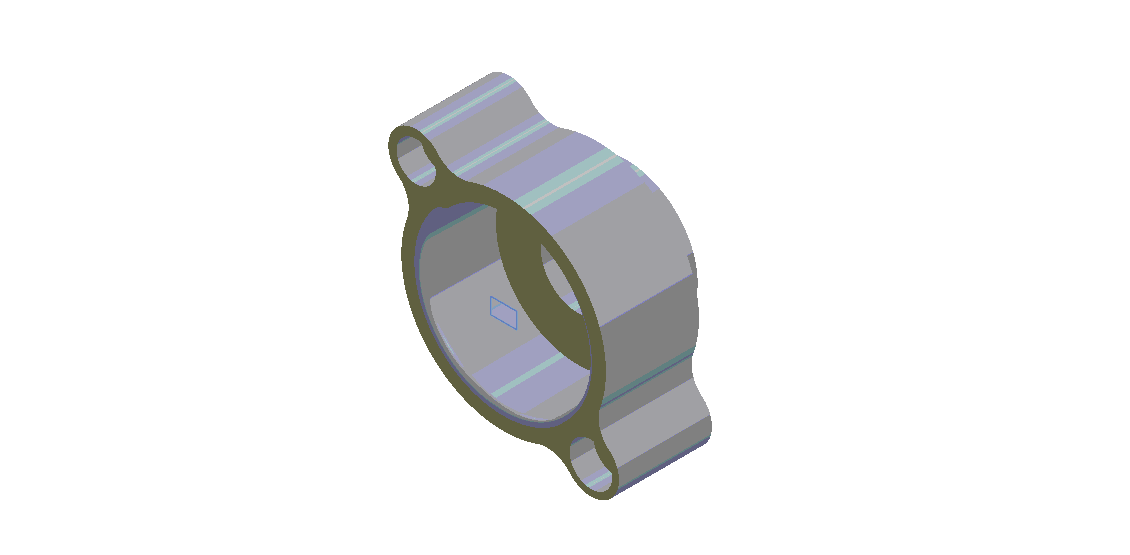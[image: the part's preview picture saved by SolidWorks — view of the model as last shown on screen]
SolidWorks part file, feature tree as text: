
SOLIDWORKS PART (.sldprt)
format: sldprt  version: not decoded by parser v0  size: 208,896 bytes
history: native  units: mm
features: sketch x8, plane x4, extrude x2, cut_extrude x2, hole x2, material x1, fillet x1 (+10 scaffold rows collapsed)
feature tree (30):
  scaffold x10  (default folders/planes/origin — collapsed)
  material  "Matériau <non spécifié>"
  plane  "FRONT"
  plane  "TOP"
  plane  "RIGHT"
  plane  "Plan1"  Offset=838.2mm
  sketch  "Esquisse1"
  extrude  "Boss.-Extru.1"  Depth=635mm
  sketch  "Esquisse2"
  extrude  "Boss.-Extru.2"  Depth=203.2mm
  sketch  "Esquisse3"
  cut_extrude  "Enlèv. mat.-Extru.1"  Depth=508mm
  sketch  "Esquisse4"
  cut_extrude  "Enlèv. mat.-Extru.2"  Depth=330.2mm
  hole  "Perçage1"  Diameter=139.7mm Depth=838.2mm
  sketch  "Esquisse6"
  sketch  "Esquisse5"  dims[Diamètre=139.7mm Profondeur=838.2mm Diamètre chambrage=292.1mm Profondeur chambrage=165.1mm]
  hole  "Perçage2"  Diameter=139.7mm Depth=838.2mm
  sketch  "Esquisse8"
  sketch  "Esquisse7"  dims[Diamètre=139.7mm Profondeur=838.2mm Diamètre chambrage=266.7mm Profondeur chambrage=165.1mm]
  fillet  "Congé1"  Radius=38.1mm
decode coverage: 9 of 15 modeling features carry decoded parameters
note: suppression state not decoded; provenance and decode notes live in map.json
